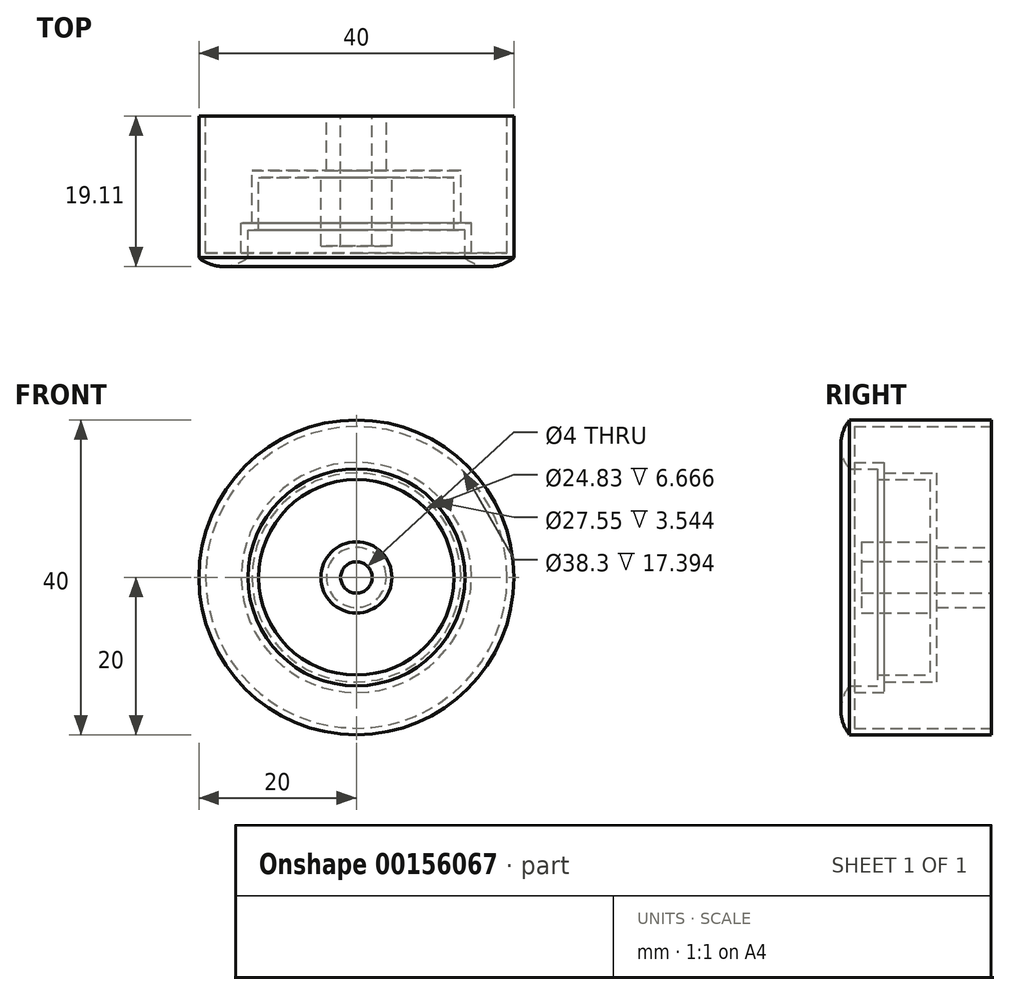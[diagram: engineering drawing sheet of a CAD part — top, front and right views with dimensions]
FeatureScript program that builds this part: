
annotation { "Feature Type Name" : "Feature", "Feature Type Description" : "" }
export const myFeature = defineFeature(function(context is Context, id is Id, definition is map)
    precondition{}
    {
        {
            var Q0;
            Q0=qCreatedBy(makeId("Top.planeOp"),FACE);
            var sketch = newSketch(context, id + "F0", { "sketchPlane" : qUnion([Q0])});
            skLineSegment(sketch, "E0", {"start": v(0, 17.4) * mm, "end": v(0, -20.43) * mm, "construction": true});
            skLineSegment(sketch, "E1", {"start": v(2, 6.54) * mm, "end": v(2, -9.96) * mm});
            skLineSegment(sketch, "E2", {"start": v(2, -9.96) * mm, "end": v(4.51, -9.96) * mm});
            skLineSegment(sketch, "E3", {"start": v(4.51, -9.96) * mm, "end": v(4.51, -1.25) * mm});
            skLineSegment(sketch, "E4", {"start": v(4.51, -1.25) * mm, "end": v(12.42, -1.25) * mm});
            skLineSegment(sketch, "E5", {"start": v(12.42, -1.25) * mm, "end": v(12.42, -7.92) * mm});
            skLineSegment(sketch, "E6", {"start": v(12.42, -7.92) * mm, "end": v(13.78, -7.92) * mm});
            skLineSegment(sketch, "E7", {"start": v(13.78, -7.92) * mm, "end": v(13.78, -11.46) * mm});
            skLineSegment(sketch, "E8", {"start": v(20, -11.46) * mm, "end": v(20, 6.54) * mm});
            skLineSegment(sketch, "E9.0", {"start": v(19.15, -10.86) * mm, "end": v(19.15, 6.54) * mm});
            skLineSegment(sketch, "E9.1", {"start": v(14.62, -10.86) * mm, "end": v(19.15, -10.86) * mm});
            skLineSegment(sketch, "E9.2", {"start": v(14.62, -7.07) * mm, "end": v(14.62, -10.86) * mm});
            skLineSegment(sketch, "E9.3", {"start": v(13.27, -7.07) * mm, "end": v(14.62, -7.07) * mm});
            skLineSegment(sketch, "E9.4", {"start": v(13.27, -0.4) * mm, "end": v(13.27, -7.07) * mm});
            skLineSegment(sketch, "E9.8", {"start": v(3.8, -0.4) * mm, "end": v(13.27, -0.4) * mm});
            skLineSegment(sketch, "E10", {"start": v(19.15, 6.54) * mm, "end": v(20, 6.54) * mm});
            skLineSegment(sketch, "E11", {"start": v(2, 6.54) * mm, "end": v(3.8, 6.54) * mm});
            skLineSegment(sketch, "E12", {"start": v(3.8, 6.54) * mm, "end": v(3.8, -0.4) * mm});
            skArc(sketch, "E13", {"start": v(13.78, -11.46) * mm, "mid": v(16.89, -12.57) * mm, "end": v(20, -11.46) * mm});
            skLineSegment(sketch, "E14", {"start": v(16.89, -10.86) * mm, "end": v(16.89, -7.65) * mm, "construction": true});
            skSolve(sketch);
        }
        {
            var Q0;
            Q0=makeQuery(id+"F0.imprint","IMPRINT",FACE,{"disambiguationData":[TD([[makeQuery(id+"F0.imprint","IMPRINT",EDGE,{"derivedFrom":sQuery(id+"F0.wireOp",EDGE,"E1")}),1.0]])]});
            var Q1;
            Q1=sQuery(id+"F0.wireOp",EDGE,"E0");
            revolve(context, id + "F1", {"entities" : qUnion([Q0]), "axis" : qUnion([Q1]), "revolveType" : RevolveType.FULL});
        }
    });
